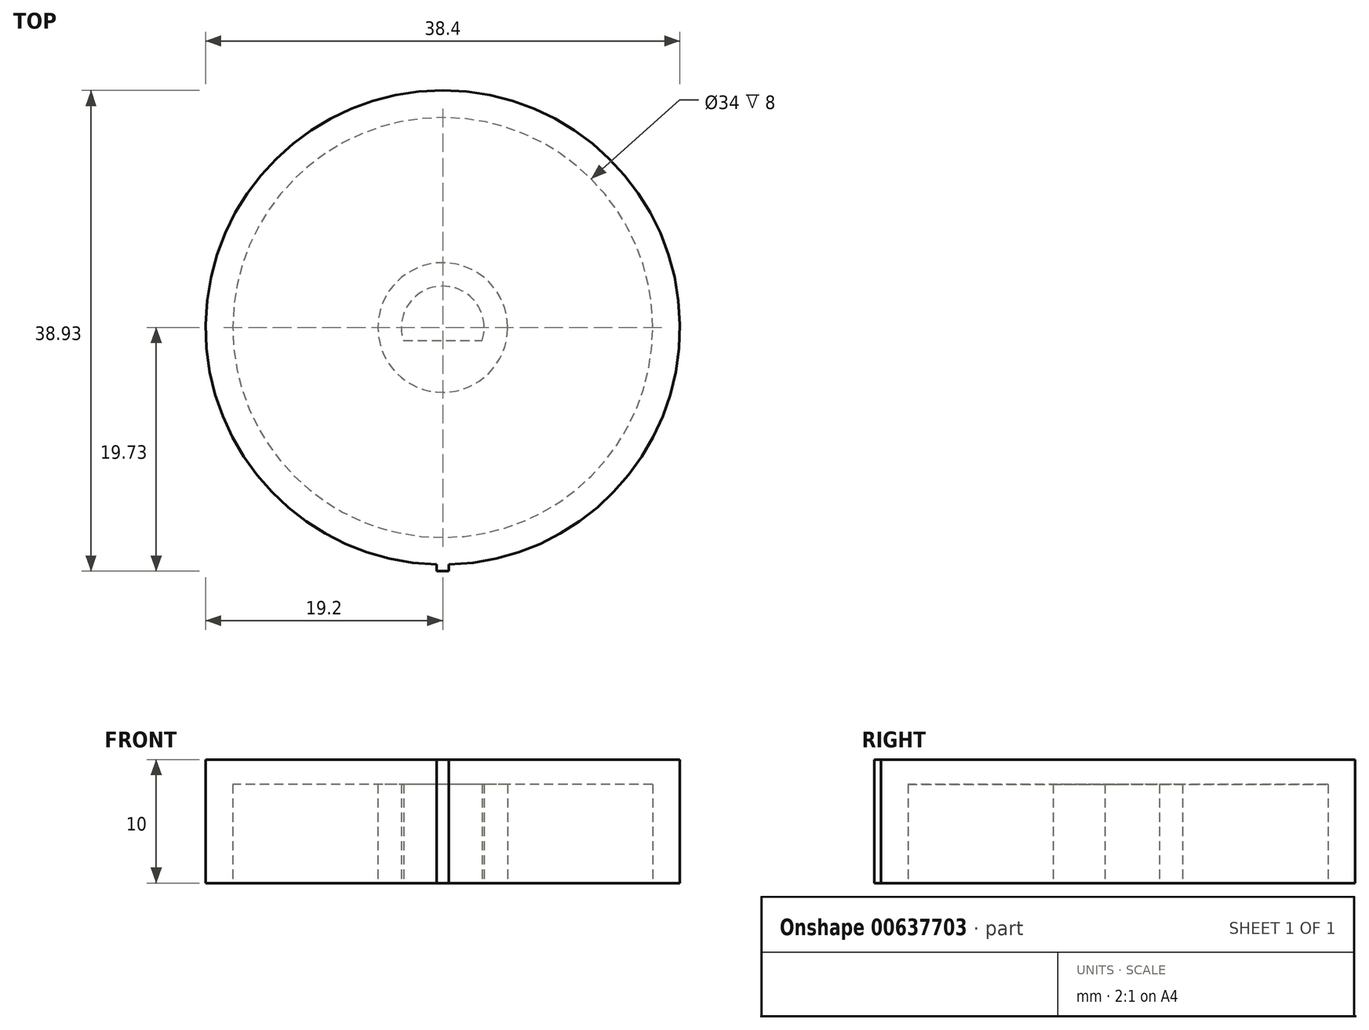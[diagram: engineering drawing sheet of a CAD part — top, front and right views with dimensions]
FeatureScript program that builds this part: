
annotation { "Feature Type Name" : "Feature", "Feature Type Description" : "" }
export const myFeature = defineFeature(function(context is Context, id is Id, definition is map)
    precondition{}
    {
        {
            var Q0;
            Q0=qCreatedBy(makeId("Top.planeOp"),FACE);
            var sketch = newSketch(context, id + "F0", { "sketchPlane" : qUnion([Q0])});
            skCircle(sketch, "E0", {"center": v(0, 0) * mm, "radius": 19.2 * mm});
            skSolve(sketch);
        }
        {
            var Q0;
            Q0=makeQuery(id+"F0.imprint","IMPRINT",FACE,{"disambiguationData":[TD([[makeQuery(id+"F0.imprint","IMPRINT",EDGE,{"derivedFrom":sQuery(id+"F0.wireOp",EDGE,"E0")}),1.0]])]});
            extrude(context, id + "F1", {"entities" : qUnion([Q0]), "depth" : 10 * mm, "offsetDistance" : 25 * mm});
        }
        {
            var Q0;
            Q0=qCreatedBy(makeId("Top.planeOp"),FACE);
            var sketch = newSketch(context, id + "F2", { "sketchPlane" : qUnion([Q0])});
            skCircle(sketch, "E1", {"center": v(0, 0) * mm, "radius": 17 * mm});
            skSolve(sketch);
        }
        {
            var Q0;
            Q0 = qSketchRegion(id + "F2", true);
            extrude(context, id + "F3", {"entities" : qUnion([Q0]), "operationType" : NewBodyOperationType.REMOVE, "depth" : 8 * mm, "offsetDistance" : 25 * mm});
        }
        {
            var Q0;
            Q0=qCreatedBy(makeId("Top.planeOp"),FACE);
            var sketch = newSketch(context, id + "F4", { "sketchPlane" : qUnion([Q0])});
            skCircle(sketch, "E2", {"center": v(0, 0) * mm, "radius": 5.25 * mm});
            skCircle(sketch, "E3", {"center": v(0, 0) * mm, "radius": 3.35 * mm});
            skSolve(sketch);
        }
        {
            var Q0;
            Q0 = qSketchRegion(id + "F4", true);
            extrude(context, id + "F5", {"entities" : qUnion([Q0]), "operationType" : NewBodyOperationType.ADD, "depth" : 10 * mm, "offsetDistance" : 25 * mm});
        }
        {
            var Q0;
            Q0=qCreatedBy(makeId("Top.planeOp"),FACE);
            var sketch = newSketch(context, id + "F6", { "sketchPlane" : qUnion([Q0])});
            skLineSegment(sketch, "E4", {"start": v(0, -5.26) * mm, "end": v(0, -1.06) * mm, "construction": true});
            skPoint(sketch, "E4.endSnap0", {"position": v(0, -3.97) * mm});
            skLineSegment(sketch, "E5", {"start": v(-4, -1.06) * mm, "end": v(4.02, -1.06) * mm});
            skArc(sketch, "E6", {"start": v(-4, -1.06) * mm, "mid": v(0.01, -3.97) * mm, "end": v(4.02, -1.06) * mm});
            skSolve(sketch);
        }
        {
            var Q0;
            Q0 = qSketchRegion(id + "F6", true);
            extrude(context, id + "F7", {"entities" : qUnion([Q0]), "operationType" : NewBodyOperationType.ADD, "depth" : 9 * mm, "offsetDistance" : 25 * mm});
        }
        {
            var Q0;
            Q0=qCreatedBy(makeId("Top.planeOp"),FACE);
            var sketch = newSketch(context, id + "F8", { "sketchPlane" : qUnion([Q0])});
            skLineSegment(sketch, "E7.bottom", {"start": v(-0.5, -19.73) * mm, "end": v(0.5, -19.73) * mm});
            skLineSegment(sketch, "E7.top", {"start": v(-0.5, -18.73) * mm, "end": v(0.5, -18.73) * mm});
            skLineSegment(sketch, "E7.left", {"start": v(-0.5, -19.73) * mm, "end": v(-0.5, -18.73) * mm});
            skLineSegment(sketch, "E7.right", {"start": v(0.5, -19.73) * mm, "end": v(0.5, -18.73) * mm});
            skPoint(sketch, "E7.middle", {"position": v(0, -19.23) * mm});
            skSolve(sketch);
        }
        {
            var Q0;
            Q0=makeQuery(id+"F8.imprint","IMPRINT",FACE,{"disambiguationData":[TD([[makeQuery(id+"F8.imprint","IMPRINT",EDGE,{"derivedFrom":sQuery(id+"F8.wireOp",EDGE,"E7.bottom")}),1.0]])]});
            extrude(context, id + "F9", {"entities" : qUnion([Q0]), "operationType" : NewBodyOperationType.ADD, "depth" : 10 * mm, "offsetDistance" : 25 * mm});
        }
    });
